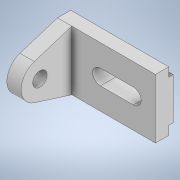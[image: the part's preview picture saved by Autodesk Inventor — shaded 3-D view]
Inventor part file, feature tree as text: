
AUTODESK INVENTOR PART (.ipt)
format: ipt  version: 2022 (Build 260153000, 153)  size: 150,016 bytes
history: native  units: mm
features: extrude x4, sketch x2, other x1
ambient origin geometry x8: Origin, YZ Plane, XZ Plane, XY Plane, X Axis, Y Axis, Z Axis, Center Point
bodies: Body1 (feature_tree)
feature tree (7):
  other  "Sólido1"
  sketch  "Esboço1"  dims[d0=89.0mm d1=54.0mm]
  extrude  "Extrusão1"  Depth=54.0mm
  extrude  "Extrusão2"  Depth=8.0mm
  extrude  "Extrusão3"  Depth=13.0mm
  extrude  "Extrusão4"  Depth=10.0mm
  sketch  "Esboço2"  dims[d2=38.0mm d3=8.0mm d4=13.0mm d5=30.0mm d6=14.0mm d8=20.0mm d9=12.0mm d10=0.0mm d11=16.0mm d12=0.0mm d13=46.0mm d14=0.0mm d15=34.0mm d16=13.0mm d17=29.0mm d18=27.0mm d19=10.0mm d20=0.0mm d21=0.5mm d22=0.872665mm]
